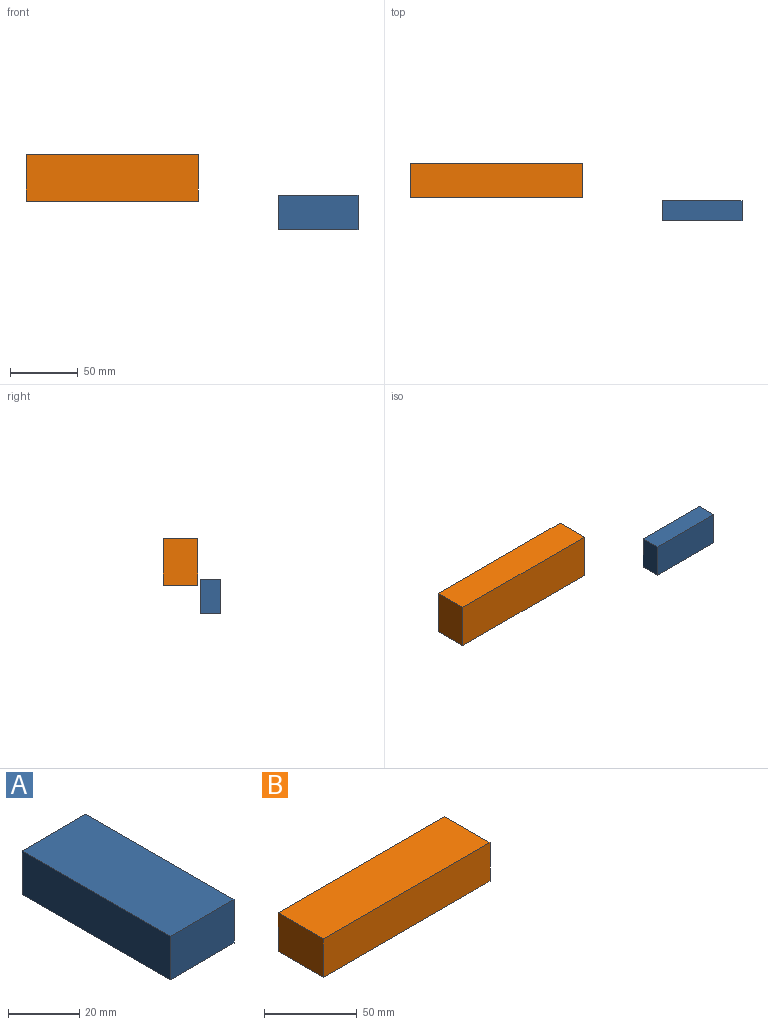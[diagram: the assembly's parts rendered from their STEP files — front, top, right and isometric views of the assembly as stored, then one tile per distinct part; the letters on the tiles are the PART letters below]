
ASSEMBLY  parts=2 mates=1
PART A: 6 faces, bbox 25.4x58.8x15 mm
  f0: plane 25.4x14.96mm, normal (0,1,0), area 379.9mm2, adj f1,f3,f4,f5
  f1: plane 58.81x25.4mm, normal (0,0,1), area 1493.6mm2, adj f0,f2,f4,f5
  f2: plane 25.4x14.96mm, normal (0,-1,0), area 379.9mm2, adj f1,f3,f4,f5
  f3: plane 58.81x25.4mm, normal (0,0,-1), area 1493.6mm2, adj f0,f2,f4,f5
  f4: plane 58.81x14.96mm, normal (1,0,0), area 879.5mm2, adj f0,f1,f2,f3
  f5: plane 58.81x14.96mm, normal (-1,0,0), area 879.5mm2, adj f0,f1,f2,f3
PART B: 6 faces, bbox 127x34.5x25.4 mm
  f0: plane 127x25.4mm, normal (0,1,0), area 3225.8mm2, adj f1,f3,f4,f5
  f1: plane 34.47x25.4mm, normal (-1,0,0), area 875.6mm2, adj f0,f2,f4,f5
  f2: plane 127x25.4mm, normal (0,-1,0), area 3225.8mm2, adj f1,f3,f4,f5
  f3: plane 34.47x25.4mm, normal (1,0,0), area 875.6mm2, adj f0,f2,f4,f5
  f4: plane 127x34.47mm, normal (0,0,1), area 4377.9mm2, adj f0,f1,f2,f3
  f5: plane 127x34.47mm, normal (0,0,-1), area 4377.9mm2, adj f0,f1,f2,f3
PLACE A rot(axis=(0.58,0.58,-0.58),120deg) t=(170.79,64.72,12.12)mm
PLACE B rot(axis=(-1,0,0),90deg) t=(0,37.96,85.29)mm
MATE parallel A.f0 <-> B.f3  axis (1,0,0) through (175.94,28.4,-0.58)mm
